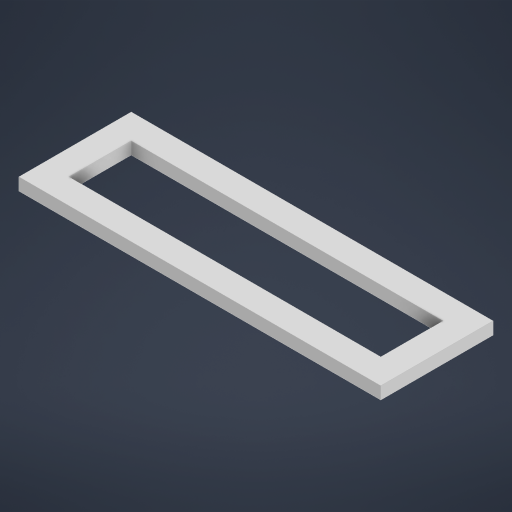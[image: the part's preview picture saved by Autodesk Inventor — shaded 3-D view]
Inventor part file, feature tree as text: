
AUTODESK INVENTOR PART (.ipt)
format: ipt  version: 2023.2 (Build 272271000, 271)  size: 206,848 bytes
history: native  units: mm
features: sketch x1
ambient origin geometry x8: Origin, YZ Plane, XZ Plane, XY Plane, X Axis, Y Axis, Z Axis, Center Point
bodies: Body1 (feature_tree)
feature tree (1):
  sketch  "Sketch1"  dims[d230=100.0mm d232=20.0mm d234=8.0mm d235=8.0mm d236=4.0mm d237=0.0mm d9=0.5mm d10=0.872665mm d11=0.5mm d12=0.872665mm d13=0.5mm d14=0.872665mm d27=0.5mm d28=0.872665mm d29=0.5mm d30=0.872665mm d88=0.5mm d89=0.872665mm d90=0.5mm d91=0.872665mm d116=0.5mm d117=0.872665mm d118=0.5mm d119=0.872665mm d154=0.5mm d155=0.872665mm d156=0.5mm d157=0.872665mm d181=0.5mm d182=0.872665mm d183=0.5mm d184=0.872665mm d221=0.5mm d222=0.872665mm d223=0.5mm d224=0.872665mm]
